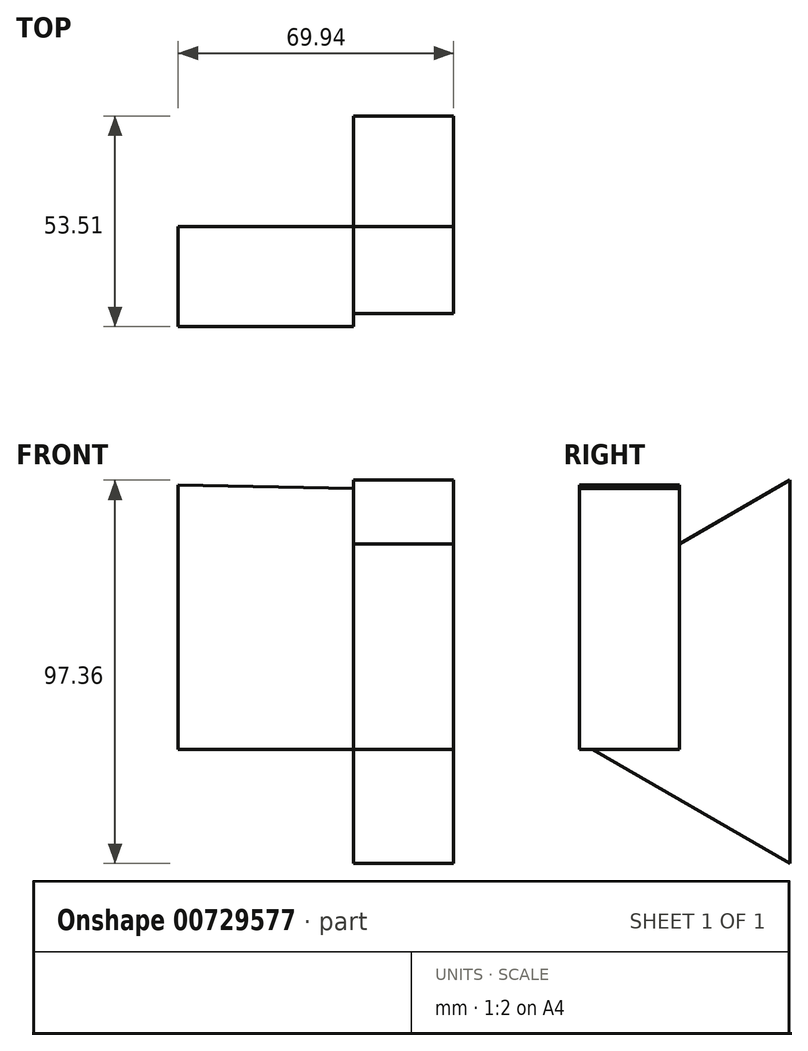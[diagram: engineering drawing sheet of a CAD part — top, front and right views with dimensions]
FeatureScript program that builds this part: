
annotation { "Feature Type Name" : "Feature", "Feature Type Description" : "" }
export const myFeature = defineFeature(function(context is Context, id is Id, definition is map)
    precondition{}
    {
        {
            var Q0;
            Q0=qCreatedBy(makeId("Front.planeOp"),FACE);
            var sketch = newSketch(context, id + "F0", { "sketchPlane" : qUnion([Q0])});
            skLineSegment(sketch, "E0", {"start": v(-51.21, 47.52) * mm, "end": v(-51.21, -19.72) * mm});
            skLineSegment(sketch, "E1", {"start": v(-51.21, -19.72) * mm, "end": v(-6.67, -19.72) * mm});
            skLineSegment(sketch, "E2", {"start": v(-6.67, -19.72) * mm, "end": v(-6.67, 46.55) * mm});
            skLineSegment(sketch, "E3", {"start": v(-51.21, 47.52) * mm, "end": v(-6.67, 46.55) * mm});
            skSolve(sketch);
        }
        {
            var Q0;
            Q0=makeQuery(id+"F0.imprint","IMPRINT",FACE,{"disambiguationData":[TD([[makeQuery(id+"F0.imprint","IMPRINT",EDGE,{"derivedFrom":sQuery(id+"F0.wireOp",EDGE,"E0")}),1.0]])]});
            var sketch = newSketch(context, id + "F1", { "sketchPlane" : qUnion([Q0])});
            skSolve(sketch);
        }
        {
            var Q0;
            Q0=makeQuery(id+"F0.imprint","IMPRINT",FACE,{"disambiguationData":[TD([[makeQuery(id+"F0.imprint","IMPRINT",EDGE,{"derivedFrom":sQuery(id+"F0.wireOp",EDGE,"E0")}),1.0]])]});
            var Q1;
            Q1=makeQuery(id+"F1.imprint","IMPRINT",FACE,{"disambiguationData":[TD([[makeQuery(id+"F1.imprint","IMPRINT",EDGE,{"derivedFrom":makeQuery(id+"F0.imprint","IMPRINT",EDGE,{"derivedFrom":sQuery(id+"F0.wireOp",EDGE,"E0")})}),1.0]])]});
            extrude(context, id + "F2", {"entities" : qUnion([Q0, Q1]), "depth" : 25.4 * mm, "offsetDistance" : 25.4 * mm});
        }
        {
            var Q0;
            {var subQ0=sQuery(id+"F0.wireOp",EDGE,"E2");Q0=makeQuery(id+"F2.opExtrude","SWEPT_FACE",FACE,{"disambiguationData":[OSD([subQ0]),TDD([makeQuery(id+"F0.imprint","IMPRINT",EDGE,{"derivedFrom":subQ0})])]});}
            var sketch = newSketch(context, id + "F3", { "sketchPlane" : qUnion([Q0])});
            skCircle(sketch, "E4.cCircle", {"center": v(0, 0) * mm, "radius": 28.1 * mm, "construction": true});
            skLineSegment(sketch, "E4.0", {"start": v(28.1, 48.68) * mm, "end": v(28.1, -48.68) * mm});
            skLineSegment(sketch, "E4.1", {"start": v(28.1, -48.68) * mm, "end": v(-56.21, 0) * mm});
            skLineSegment(sketch, "E4.2", {"start": v(-56.21, 0) * mm, "end": v(28.1, 48.68) * mm});
            skPoint(sketch, "E4.0.midPoint", {"position": v(28.1, 0) * mm});
            skSolve(sketch);
        }
        {
            var Q0;
            {var subQ8=sQuery(id+"F3.wireOp",EDGE,"E4.0");Q0=makeQuery(id+"F3.imprint","IMPRINT",FACE,{"disambiguationData":[TD([[makeQuery(id+"F3.imprint","IMPRINT",EDGE,{"derivedFrom":subQ8}),-1.0]])]});}
            extrude(context, id + "F4", {"entities" : qUnion([Q0]), "depth" : 25.4 * mm, "offsetDistance" : 25.4 * mm});
        }
    });
